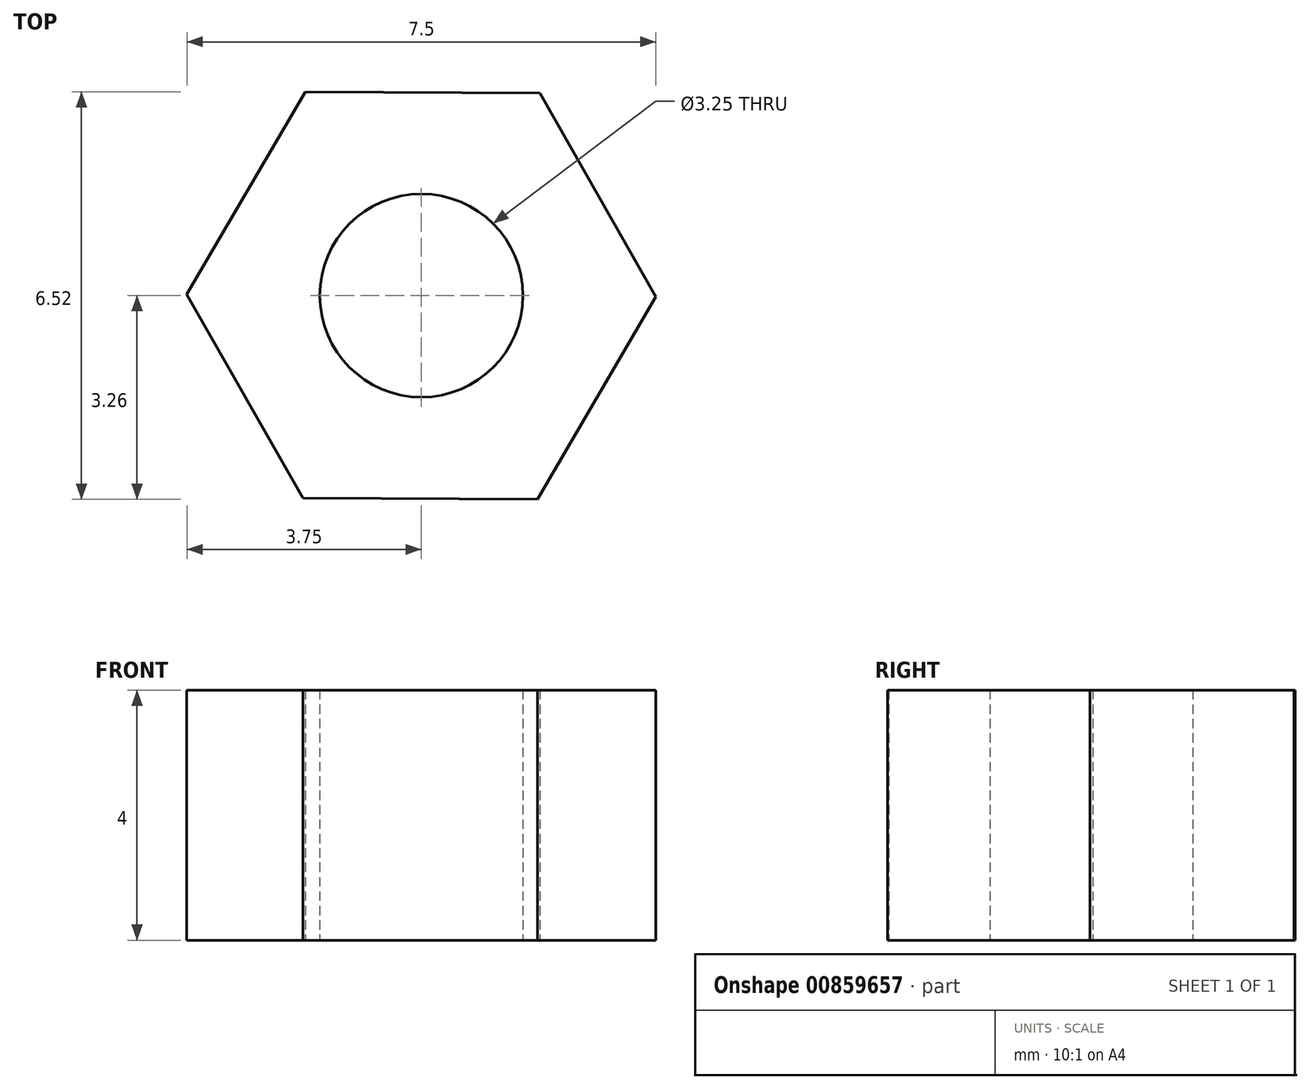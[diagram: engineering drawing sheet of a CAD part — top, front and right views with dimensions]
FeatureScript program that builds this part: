
annotation { "Feature Type Name" : "Feature", "Feature Type Description" : "" }
export const myFeature = defineFeature(function(context is Context, id is Id, definition is map)
    precondition{}
    {
        {
            var Q0;
            Q0=qCreatedBy(makeId("Top.planeOp"),FACE);
            var sketch = newSketch(context, id + "F0", { "sketchPlane" : qUnion([Q0])});
            skCircle(sketch, "E0", {"center": v(0, 0) * mm, "radius": 1.63 * mm});
            skCircle(sketch, "E1.cCircle", {"center": v(0, 0) * mm, "radius": 3.25 * mm, "construction": true});
            skLineSegment(sketch, "E1.0", {"start": v(3.75, -0.02) * mm, "end": v(1.86, -3.26) * mm});
            skLineSegment(sketch, "E1.1", {"start": v(1.86, -3.26) * mm, "end": v(-1.9, -3.24) * mm});
            skLineSegment(sketch, "E1.2", {"start": v(-1.9, -3.24) * mm, "end": v(-3.75, 0.02) * mm});
            skLineSegment(sketch, "E1.3", {"start": v(-3.75, 0.02) * mm, "end": v(-1.86, 3.26) * mm});
            skLineSegment(sketch, "E1.4", {"start": v(-1.86, 3.26) * mm, "end": v(1.9, 3.24) * mm});
            skLineSegment(sketch, "E1.5", {"start": v(1.9, 3.24) * mm, "end": v(3.75, -0.02) * mm});
            skPoint(sketch, "E1.0.midPoint", {"position": v(2.8, -1.64) * mm});
            skSolve(sketch);
        }
        {
            var Q0;
            Q0=makeQuery(id+"F0.imprint","IMPRINT",FACE,{"disambiguationData":[TD([[makeQuery(id+"F0.imprint","IMPRINT",EDGE,{"derivedFrom":sQuery(id+"F0.wireOp",EDGE,"E0")}),-1.0]])]});
            extrude(context, id + "F1", {"entities" : qUnion([Q0]), "depth" : 4 * mm, "offsetDistance" : 25 * mm});
        }
    });
